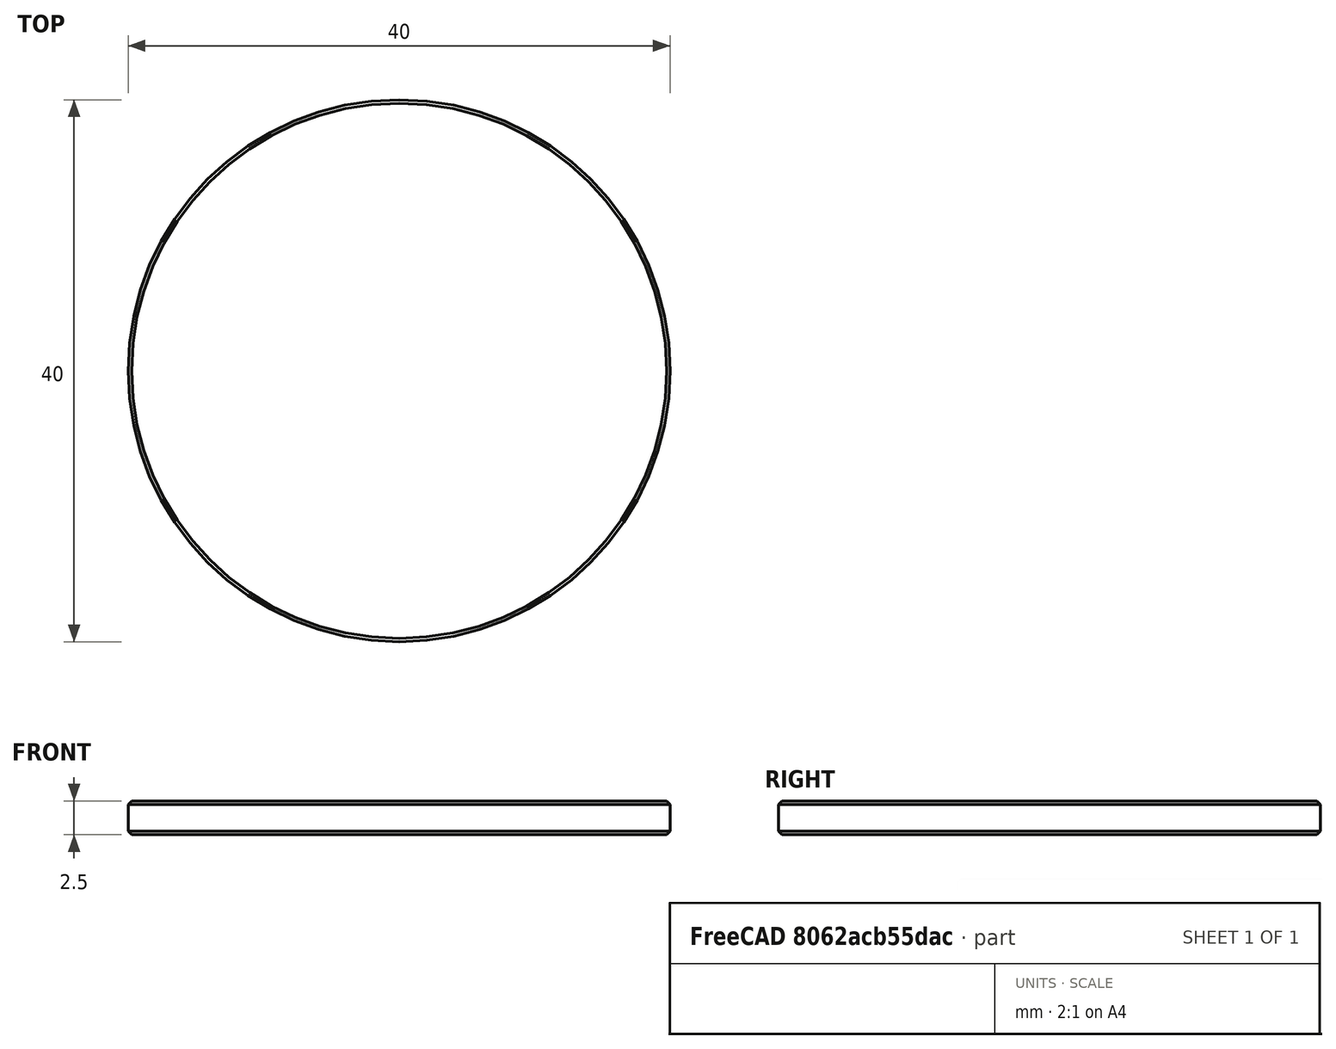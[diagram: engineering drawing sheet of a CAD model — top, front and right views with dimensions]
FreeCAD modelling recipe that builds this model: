
FCSTD DOCUMENT  (FreeCAD 0.20R29603 (Git))
Label: blank-coin
License: All rights reserved
LicenseURL: http://en.wikipedia.org/wiki/All_rights_reserved
objects: Sketcher::SketchObject×4, App::DocumentObjectGroup×3, PartDesign::Plane×2, App::TextDocument×1, Spreadsheet::Sheet×1, PartDesign::Revolution×1, PartDesign::Body×1
note: 9 computed .brp shape members not serialized (recipe doc carries the construction recipe); baked Part::Feature solids carry a one-line shape summary decoded from their .brp

FEATURE [App::TextDocument] Text_document  label="Text document"
FEATURE [Spreadsheet::Sheet] Spreadsheet
  cells = A2=Vector X center; B2=vec_x; C2(dim_vec_x)==-14 mm; A3=Vector Y center; B3=vec_y; C3(dim_vec_y)==14 mm; A4=Coin radius; B4=coin_r; C4(dim_coin_r)==20 mm; A5=Coin height; B5=coin_h; C5(dim_coin_h)==2.5 mm; D5==2.5 mm; A6=Engrave depth; B6=engrave_h; C6(dim_engrave_h)==dim_coin_h / 2; A7=Chamfer width; B7=chamfer_w; C7(dim_chamfer_w)==dim_coin_h / 10; A8=Chamfer radius; B8=chamfer_r; C8(dim_chamfer_r)==dim_coin_r - dim_chamfer_w; A9=SVG Scale; B9=svg_scale; C9=0.2; A11=Edge dimple radius; B11=dimple_r; C11(dim_dimple_r)==0.5 mm; A12=Edge dimple count; B12=dimple_count; C12(dim_dimple_count)=64
FEATURE [PartDesign::Plane] DatumPlane  label="BaseXYDatumPlane"
  Length = 60
  MapMode = 5
  ResizeMode = 0
  Support = -> [XY_Plane]
  Width = 60
FEATURE [Sketcher::SketchObject] Sketch001  label="CircleSketch"
  FullyConstrained = true
  MapMode = 5
  Support = -> [DatumPlane]
  expr: Constraints[1] = Spreadsheet.dim_coin_r - Spreadsheet.dim_chamfer_w
  expr: Constraints[3] = Spreadsheet.dim_coin_r - 1 mm
  sketch-geometry (6):
    g0: Circle CenterX=0 CenterY=0 CenterZ=0 NormalX=0 NormalY=0 NormalZ=1 AngleXU=0 Radius=19.75
    g1: Circle CenterX=0 CenterY=0 CenterZ=0 NormalX=0 NormalY=0 NormalZ=1 AngleXU=0 Radius=19
    g2: LineSegment StartX=0 StartY=0 StartZ=0 EndX=0 EndY=19 EndZ=0
    g3: LineSegment StartX=0 StartY=0 StartZ=0 EndX=0 EndY=-19 EndZ=0
    g4: LineSegment StartX=0 StartY=0 StartZ=0 EndX=-19 EndY=0 EndZ=0
    g5: LineSegment StartX=0 StartY=0 StartZ=0 EndX=19 EndY=0 EndZ=0
  constraints (16):
    c: Coincident(g0,g-1)
    c: Radius(g0) = 19.75
    c: Coincident(g1,g0)
    c: Radius(g1) = 19
    c: Coincident(g2,g0)
    c: PointOnObject(g2,g1)
    c: Vertical(g2)
    c: Coincident(g3,g0)
    c: PointOnObject(g3,g1)
    c: Vertical(g3)
    c: Coincident(g4,g0)
    c: PointOnObject(g4,g1)
    c: Horizontal(g4)
    c: Coincident(g5,g0)
    c: PointOnObject(g5,g1)
    c: Horizontal(g5)
FEATURE [PartDesign::Plane] DatumPlane001  label="ProfileYZDatumPlane"
  Length = 60
  MapMode = 5
  Placement = pos=(0,0,0) rot=(0.57735,0.57735,0.57735;2.0944rad)
  ResizeMode = 0
  Support = -> [YZ_Plane]
  Width = 60
FEATURE [Sketcher::SketchObject] Sketch  label="CoinProfileSketch"
  FullyConstrained = true
  MapMode = 5
  Placement = pos=(0,0,0) rot=(0.57735,0.57735,0.57735;2.0944rad)
  Support = -> [DatumPlane001]
  expr: Constraints[10] = Spreadsheet.dim_chamfer_w
  expr: Constraints[12] = Spreadsheet.dim_coin_h
  expr: Constraints[13] = Spreadsheet.dim_coin_r
  expr: Constraints[14] = Spreadsheet.dim_coin_r
  expr: Constraints[15] = Spreadsheet.dim_coin_h
  expr: Constraints[16] = Spreadsheet.dim_chamfer_r
  sketch-geometry (11):
    g0: LineSegment StartX=0 StartY=0 StartZ=0 EndX=0 EndY=-2.5 EndZ=0
    g1: LineSegment StartX=19.75 StartY=0 StartZ=0 EndX=20 EndY=-0.25 EndZ=0
    g2: LineSegment StartX=20 StartY=-0.25 StartZ=0 EndX=20 EndY=-2.25 EndZ=0
    g3: LineSegment StartX=20.25 StartY=0 StartZ=0 EndX=20 EndY=0 EndZ=0
    g4: LineSegment StartX=20 StartY=0 StartZ=0 EndX=20 EndY=-0.25 EndZ=0
    g5: LineSegment StartX=20 StartY=-2.25 StartZ=0 EndX=20 EndY=-2.5 EndZ=0
    g6: LineSegment StartX=0 StartY=0 StartZ=0 EndX=19.75 EndY=0 EndZ=0
    g7: LineSegment StartX=19.75 StartY=0 StartZ=0 EndX=20 EndY=0 EndZ=0
    g8: LineSegment StartX=20 StartY=-2.5 StartZ=0 EndX=19.75 EndY=-2.5 EndZ=0
    g9: LineSegment StartX=19.75 StartY=-2.5 StartZ=0 EndX=0 EndY=-2.5 EndZ=0
    g10: LineSegment StartX=19.75 StartY=-2.5 StartZ=0 EndX=20 EndY=-2.25 EndZ=0
  constraints (31):
    c: Vertical(g0)
    c: Coincident(g1,g2)
    c: Vertical(g2)
    c: Horizontal(g3)
    c: Coincident(g4,g3)
    c: Coincident(g4,g1)
    c: Coincident(g5,g2)
    c: Vertical(g5)
    c: Vertical(g4)
    c: Equal(g3,g4)
    c: DistanceY(g5,g5) = 0.25
    c: Equal(g5,g4)
    c: DistanceY(g5,g3) = 2.5
    c: DistanceX(g0,g5) = 20
    c: DistanceX(g-1,g3) = 20
    c: DistanceY(g0,g-1) = 2.5
    c: DistanceX(g1) = 19.75
    c: Coincident(g6,g0)
    c: Coincident(g6,g1)
    c: Horizontal(g6)
    c: Coincident(g7,g1)
    c: Coincident(g7,g3)
    c: Horizontal(g7)
    c: Coincident(g8,g5)
    c: Horizontal(g8)
    c: Coincident(g9,g8)
    c: Coincident(g9,g0)
    c: Horizontal(g9)
    c: Coincident(g10,g9)
    c: Coincident(g10,g2)
    c: Equal(g9,g6)
FEATURE [PartDesign::Revolution] Revolution  label="CoinRevolution"
  Angle = 360
  Axis = (-1e-16,1e-16,1)
  Base = (0,0,0)
  Placement = pos=(0,0,0) rot=(0.57735,0.57735,0.57735;2.0944rad)
  Profile = -> Sketch
  ReferenceAxis = -> Sketch [V_Axis]
  Reversed = true
FEATURE [Sketcher::SketchObject] Sketch002  label="CoinEdgeProfileSketch"
  FullyConstrained = true
  MapMode = 5
  Placement = pos=(0,0,0) rot=(0.57735,0.57735,0.57735;2.0944rad)
  Support = -> [DatumPlane001]
  expr: Constraints[10] = Spreadsheet.dim_coin_r
  expr: Constraints[11] = Spreadsheet.dim_coin_h
  expr: Constraints[17] = Spreadsheet.dim_chamfer_r
  expr: Constraints[6] = Spreadsheet.dim_chamfer_w
  expr: Constraints[8] = Spreadsheet.dim_coin_h
  expr: Constraints[9] = Spreadsheet.dim_coin_r
  sketch-geometry (13):
    g0: LineSegment StartX=0 StartY=2e-16 StartZ=0 EndX=0 EndY=-2.5 EndZ=0
    g1: LineSegment StartX=20 StartY=-0.25 StartZ=0 EndX=20 EndY=-2.25 EndZ=0
    g2: LineSegment StartX=20 StartY=2e-16 StartZ=0 EndX=20 EndY=-0.25 EndZ=0
    g3: LineSegment StartX=20 StartY=-2.25 StartZ=0 EndX=20 EndY=-2.5 EndZ=0
    g4: LineSegment StartX=0 StartY=2e-16 StartZ=0 EndX=19 EndY=2e-16 EndZ=0
    g5: LineSegment StartX=19 StartY=2e-16 StartZ=0 EndX=19 EndY=-2.5 EndZ=0
    g6: LineSegment StartX=19 StartY=2e-16 StartZ=0 EndX=19.75 EndY=2e-16 EndZ=0
    g7: LineSegment StartX=19.75 StartY=2e-16 StartZ=0 EndX=20 EndY=-0.25 EndZ=0
    g8: LineSegment StartX=19.75 StartY=2e-16 StartZ=0 EndX=20 EndY=2e-16 EndZ=0
    g9: LineSegment StartX=20 StartY=-2.5 StartZ=0 EndX=19.75 EndY=-2.5 EndZ=0
    g10: LineSegment StartX=19 StartY=-2.5 StartZ=0 EndX=0 EndY=-2.5 EndZ=0
    g11: LineSegment StartX=19.75 StartY=-2.5 StartZ=0 EndX=20 EndY=-2.25 EndZ=0
    g12: LineSegment StartX=19.75 StartY=-2.5 StartZ=0 EndX=19 EndY=-2.5 EndZ=0
  constraints (36):
    c: Vertical(g0)
    c: Coincident(g0,g4)
    c: Vertical(g1)
    c: Coincident(g3,g1)
    c: Vertical(g3)
    c: Vertical(g2)
    c: DistanceY(g3,g3) = 0.25
    c: Equal(g3,g2)
    c: DistanceY(g3,g2) = 2.5
    c: DistanceX(g0,g3) = 20
    c: DistanceX(g-1,g2) = 20
    c: DistanceY(g0,g-1) = 2.5
    c: Horizontal(g4)
    c: Vertical(g5)
    c: DistanceX(g4,g2) = 1
    c: Coincident(g6,g5)
    c: Horizontal(g6)
    c: DistanceX(g0,g6) = 19.75
    c: Coincident(g7,g6)
    c: Coincident(g7,g1)
    c: Coincident(g8,g6)
    c: Coincident(g8,g2)
    c: Horizontal(g8)
    c: Coincident(g4,g5)
    c: Coincident(g2,g1)
    c: Coincident(g9,g3)
    c: Horizontal(g9)
    c: Coincident(g10,g5)
    c: Coincident(g10,g0)
    c: Horizontal(g10)
    c: Coincident(g11,g9)
    c: Coincident(g11,g1)
    c: Coincident(g12,g11)
    c: Coincident(g12,g5)
    c: Horizontal(g12)
    c: Equal(g12,g6)
FEATURE [Sketcher::SketchObject] Sketch004  label="EdgeDimpleSketch"
  FullyConstrained = true
  MapMode = 5
  Support = -> [DatumPlane]
  expr: Constraints[2] = Spreadsheet.dim_coin_r
  sketch-geometry (2):
    g0: LineSegment StartX=0 StartY=0 StartZ=0 EndX=20 EndY=0 EndZ=0
    g1: Circle CenterX=20 CenterY=0 CenterZ=0 NormalX=0 NormalY=0 NormalZ=1 AngleXU=0 Radius=0.5
  constraints (5):
    c: Horizontal(g0)
    c: Coincident(g1,g0)
    c: DistanceX(g0,g0) = 20
    c: Coincident(g0,g-1)
    c: Radius(g1) = 0.5
FEATURE [PartDesign::Body] Body
  Group = -> [DatumPlane,Sketch001,DatumPlane001,Sketch,Revolution,Sketch002,Sketch004]
  Origin = -> Origin
  Tip = -> Revolution
FEATURE [App::DocumentObjectGroup] Group007  label="VectorOutlineGroup"
FEATURE [App::DocumentObjectGroup] Group008  label="VectorDetailGroup"
FEATURE [App::DocumentObjectGroup] Group  label="ResizeGroup"
